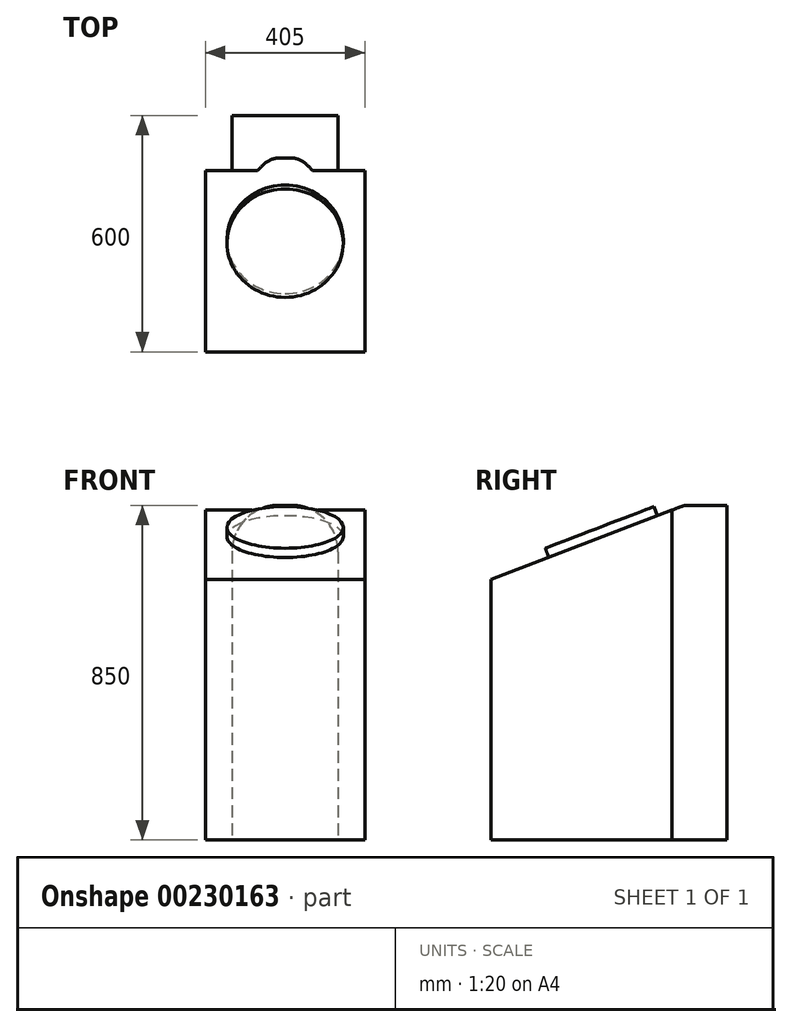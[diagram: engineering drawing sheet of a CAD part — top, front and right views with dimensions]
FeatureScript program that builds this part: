
annotation { "Feature Type Name" : "Feature", "Feature Type Description" : "" }
export const myFeature = defineFeature(function(context is Context, id is Id, definition is map)
    precondition{}
    {
        {
            var Q0;
            Q0=qCreatedBy(makeId("Top.planeOp"),FACE);
            var sketch = newSketch(context, id + "F0", { "sketchPlane" : qUnion([Q0])});
            skLineSegment(sketch, "E0.bottom", {"start": v(202.5, 230) * mm, "end": v(-202.5, 230) * mm});
            skLineSegment(sketch, "E0.top", {"start": v(202.5, -230) * mm, "end": v(-202.5, -230) * mm});
            skLineSegment(sketch, "E0.left", {"start": v(202.5, 230) * mm, "end": v(202.5, -230) * mm});
            skLineSegment(sketch, "E0.right", {"start": v(-202.5, 230) * mm, "end": v(-202.5, -230) * mm});
            skPoint(sketch, "E0.middle", {"position": v(0, 0) * mm});
            skLineSegment(sketch, "E1.bottom", {"start": v(134.78, 230) * mm, "end": v(-134.78, 230) * mm});
            skLineSegment(sketch, "E1.top", {"start": v(134.78, 370) * mm, "end": v(-134.78, 370) * mm});
            skLineSegment(sketch, "E1.left", {"start": v(134.78, 230) * mm, "end": v(134.78, 370) * mm});
            skLineSegment(sketch, "E1.right", {"start": v(-134.78, 230) * mm, "end": v(-134.78, 370) * mm});
            skPoint(sketch, "E1.middle", {"position": v(0, 300) * mm});
            skSolve(sketch);
        }
        {
            var Q0;
            Q0 = qSketchRegion(id + "F0", true);
            extrude(context, id + "F1", {"entities" : qUnion([Q0]), "depth" : 850 * mm});
        }
        {
            var Q0;
            Q0=makeQuery(id+"F1.opExtrude","SWEPT_FACE",FACE,{"disambiguationData":[OSD([sQuery(id+"F0.wireOp",EDGE,"E0.left")])]});
            var sketch = newSketch(context, id + "F2", { "sketchPlane" : qUnion([Q0])});
            skLineSegment(sketch, "E2", {"start": v(364.74, 889.2) * mm, "end": v(-312.2, 629.45) * mm});
            skLineSegment(sketch, "E3", {"start": v(-312.2, 629.45) * mm, "end": v(-312.2, 956.11) * mm});
            skLineSegment(sketch, "E4", {"start": v(-312.2, 956.11) * mm, "end": v(364.74, 889.2) * mm});
            skSolve(sketch);
        }
        {
            var Q0;
            Q0 = qSketchRegion(id + "F2", true);
            extrude(context, id + "F3", {"entities" : qUnion([Q0]), "operationType" : NewBodyOperationType.REMOVE, "endBound" : BoundingType.THROUGH_ALL, "oppositeDirection" : true, "depth" : 25 * mm});
        }
        {
            var Q0;
            Q0=makeQuery(id+"F1.opExtrude","CAP_EDGE",EDGE,{"disambiguationData":[OSD([sQuery(id+"F0.wireOp",EDGE,"E1.left")])],"isStart":false});
            var Q1;
            Q1=makeQuery(id+"F1.opExtrude","CAP_EDGE",EDGE,{"disambiguationData":[OSD([sQuery(id+"F0.wireOp",EDGE,"E1.right")])],"isStart":false});
            fillet(context, id + "F4", {"entities" : qUnion([Q0, Q1]), "radius" : 118.3 * mm, "tangentPropagation" : true, "allowEdgeOverflow" : false});
        }
        {
            var Q0;
            Q0=makeQuery(id+"F3.boolean.opBoolean","COPY",FACE,{"derivedFrom":makeQuery(id+"F3.opExtrude","SWEPT_FACE",FACE,{"disambiguationData":[OSD([sQuery(id+"F2.wireOp",EDGE,"E2")])]})});
            var sketch = newSketch(context, id + "F5", { "sketchPlane" : qUnion([Q0])});
            skCircle(sketch, "E5", {"center": v(0, 327.74) * mm, "radius": 147.77 * mm});
            skSolve(sketch);
        }
        {
            var Q0;
            Q0 = qSketchRegion(id + "F5", true);
            extrude(context, id + "F6", {"entities" : qUnion([Q0]), "operationType" : NewBodyOperationType.ADD, "depth" : 25 * mm});
        }
    });
